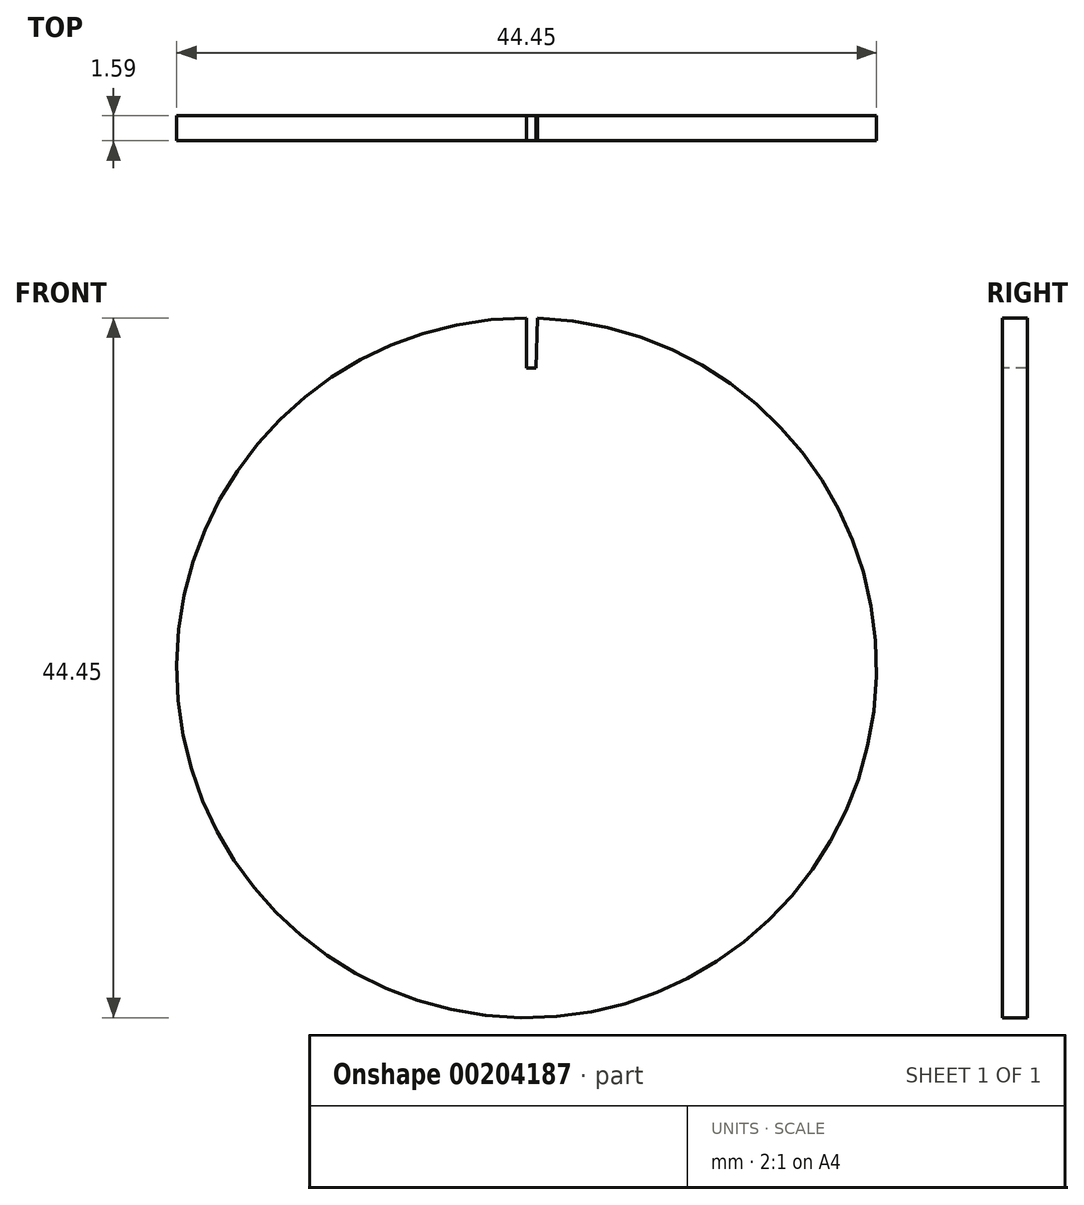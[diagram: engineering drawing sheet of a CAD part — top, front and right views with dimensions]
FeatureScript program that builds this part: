
annotation { "Feature Type Name" : "Feature", "Feature Type Description" : "" }
export const myFeature = defineFeature(function(context is Context, id is Id, definition is map)
    precondition{}
    {
        {
            var Q0;
            Q0=qCreatedBy(makeId("Front.planeOp"),FACE);
            var sketch = newSketch(context, id + "F0", { "sketchPlane" : qUnion([Q0])});
            skCircle(sketch, "E0", {"center": v(0, 0) * mm, "radius": 22.23 * mm});
            skLineSegment(sketch, "E1.anchor1", {"start": v(0, 0) * mm, "end": v(0, 0) * mm});
            skLineSegment(sketch, "E1.anchor2", {"start": v(0, 0) * mm, "end": v(0, 0) * mm});
            skCircle(sketch, "E2", {"center": v(0, 0) * mm, "radius": 19.05 * mm});
            skLineSegment(sketch, "E3", {"start": v(0, 19.05) * mm, "end": v(0, 22.23) * mm});
            skLineSegment(sketch, "E4", {"start": v(0.6, 19.04) * mm, "end": v(0.7, 22.21) * mm});
            skSolve(sketch);
        }
        {
            var Q0;
            {var subQ0=sQuery(id+"F0.wireOp",EDGE,"E3");Q0=makeQuery(id+"F0.imprint","IMPRINT",FACE,{"disambiguationData":[TD([[makeQuery(id+"F0.imprint","IMPRINT",EDGE,{"derivedFrom":subQ0}),1.0]])]});}
            var Q1;
            {var subQ0=sQuery(id+"F0.wireOp",EDGE,"E2");var subQ1=makeQuery(id+"F0.imprint","INTERSECT",VERTEX,{"derivedFrom":[subQ0,sQuery(id+"F0.wireOp",EDGE,"E3")]});Q1=makeQuery(id+"F0.imprint","IMPRINT",FACE,{"disambiguationData":[TD([[makeQuery(id+"F0.imprint","IMPRINT",EDGE,{"disambiguationData":[TD([[subQ1,1.0]])],"derivedFrom":subQ0}),1.0]])]});}
            var Q2;
            {var subQ0=sQuery(id+"F0.wireOp",EDGE,"E3");Q2=makeQuery(id+"F0.imprint","IMPRINT",FACE,{"disambiguationData":[TD([[makeQuery(id+"F0.imprint","IMPRINT",EDGE,{"derivedFrom":subQ0}),-1.0]])]});}
            extrude(context, id + "F1", {"entities" : qUnion([Q0, Q1, Q2]), "oppositeDirection" : true, "depth" : 1.59 * mm});
        }
        {
            var Q0;
            {var subQ0=sQuery(id+"F0.wireOp",EDGE,"E3");Q0=makeQuery(id+"F0.imprint","IMPRINT",FACE,{"disambiguationData":[TD([[makeQuery(id+"F0.imprint","IMPRINT",EDGE,{"derivedFrom":subQ0}),-1.0]])]});}
            extrude(context, id + "F2", {"entities" : qUnion([Q0]), "operationType" : NewBodyOperationType.REMOVE, "oppositeDirection" : true, "depth" : 25.4 * mm});
        }
    });
